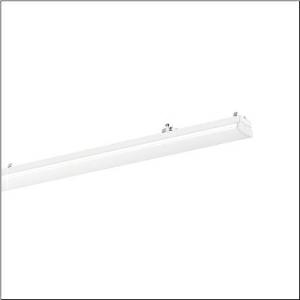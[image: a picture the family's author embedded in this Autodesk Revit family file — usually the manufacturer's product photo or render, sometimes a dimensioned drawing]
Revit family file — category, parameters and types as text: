
# Revit family: licross_r__21_recessed_opal_mo_52tl1ddv4e5g_bd2f
name_source: partatom
category: Lighting Fixtures
units: mm (PartAtom-declared; Revit-internal decimal feet)

## family parameters
Cut with Voids When Loaded = No
Host = Face
Light Source = No
Part Type = Normal
Room Calculation Point = No
Round Connector Dimension = Use Diameter
Shared = No

## types (1)
- --- (1 x LED, 14620 lm, 85.3 W, 4000K)
    Apparent Load = 85 VA
    CIE Flux Codes = 44 73 91 87 100
    Color Rendering = 80
    Color Temperature = 4000K
    Default Elevation = 1800 mm
    Description = Licross® 21 recessed opal MO, luminaire insert, of sheet steel, galvanised, coil coated, white, length: 2.250mm, width: 66mm, height: 67mm, LED rated luminous flux: 14.620lm, light colour: 840, control gear: DALI 2, with plug, 5-pole, with phase selection, mains connection: 220..240V, AC, 50/60Hz, rated input power: 85W, halogen-free wiring, primary optical cover: cover, of PMMA, light emission: direct with ceiling illumination distribution, primary light characteristic: symmetric, protection rating (complete): IP40, insulation class (complete): insulation class I (protective earthing), certification: CE, ENEC, VDE, UKCA, protection symbol: D if used in an environment without relevant dust loads with corresponding accessories, impact resistance: IK06, permissible ambient temperature for indoor applications: -25..+35°C, corresponds to IFS (International Featured Standards) requirements for safety and quality in the food industry, reducing of maximum allowable ambient temperature of 5°C with ceiling mounting, LABS conformity tested according to VDMA 24364:2018-05, packaging unit: 1 piece
    Height = 83 mm
    Lamp = 1 x LED
    Lamp Light Flux = 14620 lm
    Lamp Power = 85.3 W
    Lamp count = 1
    Length = 2250 mm
    Luminous efficacy = 171 lm/W
    Manufacturer = Siteco
    ModVariant = No
    Model = 52TL1DDV4E5G
    Mounting Place = Ceiling
    Mounting Type = Pendant
    Number of Poles = 1
    OnlyDefault = Yes
    Power Factor = 1
    Product Name = Licross® 21 recessed opal MO
    Product group = luminaire insert
    ProductGroupID = 902
    Protection Class = Protection class I
    Protection Degree = IP 40
    RLX_Detail_Level = 1
    RLX_Emergency_Light_Flux = 0 lm
    RLX_Emergency_Type = 0
    RLX_Emergency_Type_DB = No
    RlxData = <blob elided: 27181 chars, md5=eff66cc2>
    Socket = socket
    Standby Power = 0 W
    System Light Flux = 14620 lm
    System Power = 85 W
    Type Comments = factory setting: luminous flux: 100 % | dim-lin: 254 | 390 mA
    Type Image = l_1313666.jpg
    URL = http://relux.com
    VarID = @adj_065102
    Voltage = 0 V
    Weight = 0.00 kg
    Width = 76 mm

## geometry (parser evidence)
native form markers: Blend x4, Sweep x14
no freeform markers — native parametric forms only
